# Revit family: Fold Wall
name_source: partatom
category: Lighting Fixtures
revit_build: Autodesk Revit 2018 (Build: 20170223_1515(x64)
units: mm (PartAtom-declared; Revit-internal decimal feet)

## family parameters
Always vertical = Yes
Cut with Voids When Loaded = No
Host = Wall
Light Source = Yes
OmniClass Number = 23.80.70.00
OmniClass Title = Lighting
Part Type = Normal
Room Calculation Point = No
Round Connector Dimension = Use Diameter
Shared = No

## types (2) — shared parameters
Color Filter = 16777215
Dimming Lamp Color Temperature Shift = <None>
Driver Required = No
Manufacturer = Astro Lighting Ltd
URL = www.astrolighting.com

## per-type parameters (varying)
| type | ADA compliant | Apparent Load | Dimmable | Driver Included | Efficacy (lm/w) | Electrical Class | Emit from Line Length | Lamp | Light Source Fixed | Light Source Symbol Length | Location rating | Main Finish | Main Material | Power (Watts) | Product Code | Product Location | Product Name | Product SKU | Spot Beam Angle | Spot Field Angle | Tilt Angle |
| CE |  | 11 VA | Non-Dimming | Yes | 30 | 1 | 25 mm  [stored 0.082021 ft] | Citizen CL-L104 | Adjustable | 1500 mm  [stored 4.92126 ft] | Zone 3 | Matt Nickel | Metal - Aluminium | 3 | 8610 | Indoor | Fold Wall LED | 1408003 | 60.00° | 60.00° | 90.00° |
| ETL | NO | 0 VA |  |  |  | 0 | 610 mm |  |  | 3048 mm  [stored 10 ft] | DAMP |  | Metal - Steel |  | 1234 | Bathroom |  | 1234001 | 30.00° | 90.00° | 60.00° |

note: [stored X ft] marks values corroborated as IEEE doubles in the binary element streams (Revit-internal decimal feet)

## geometry (parser evidence)
native form markers: Sweep x2
no freeform markers — native parametric forms only
